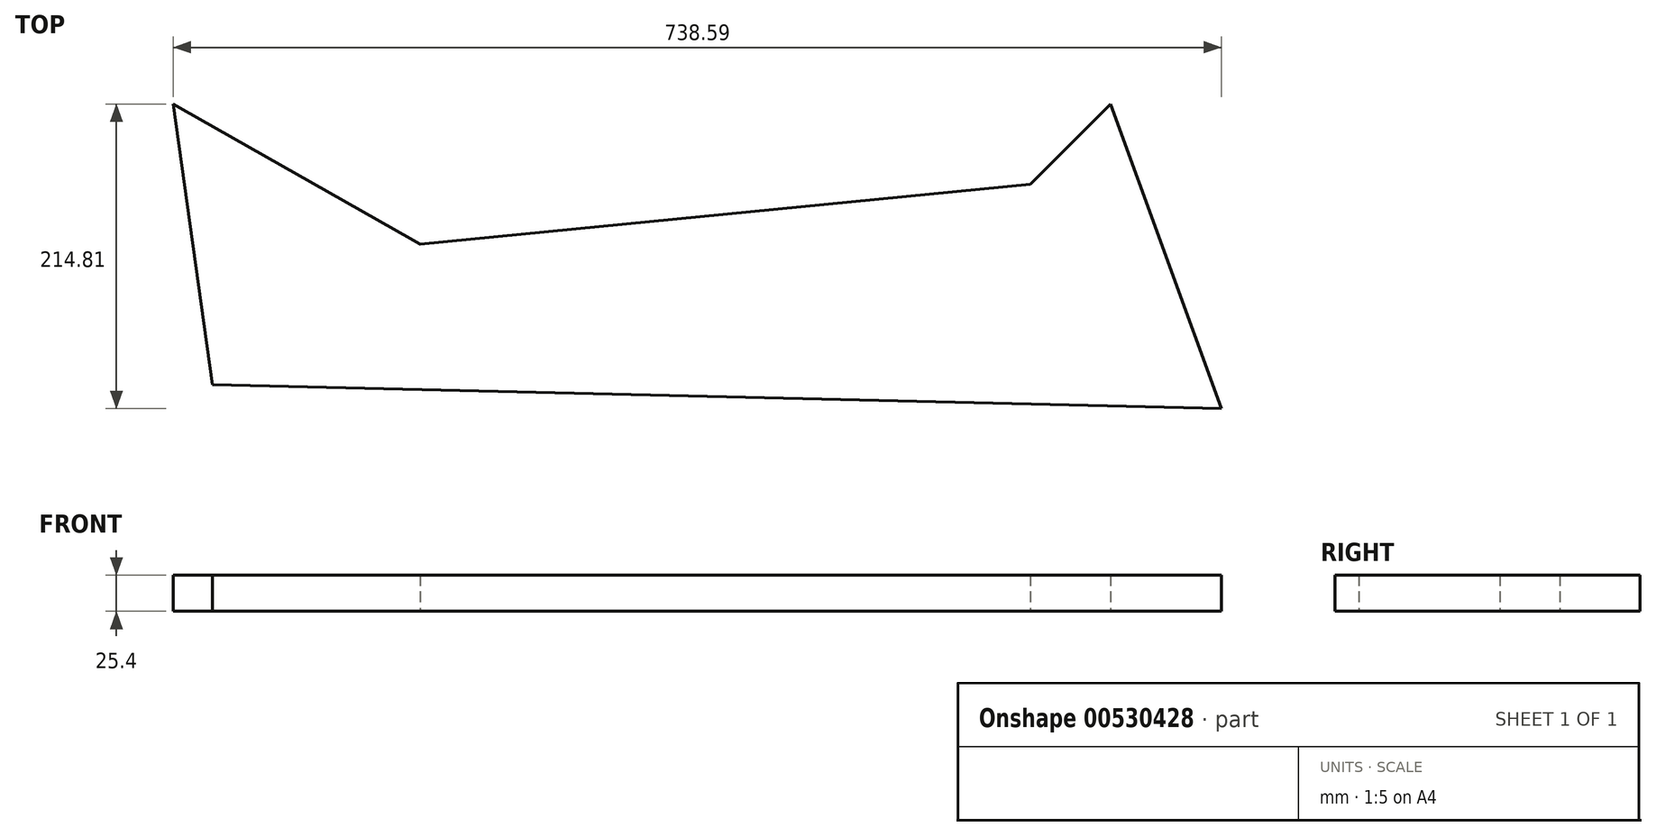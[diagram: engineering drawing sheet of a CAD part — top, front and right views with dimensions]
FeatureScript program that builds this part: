
annotation { "Feature Type Name" : "Feature", "Feature Type Description" : "" }
export const myFeature = defineFeature(function(context is Context, id is Id, definition is map)
    precondition{}
    {
        {
            var Q0;
            Q0=qCreatedBy(makeId("Top.planeOp"),FACE);
            var sketch = newSketch(context, id + "F0", { "sketchPlane" : qUnion([Q0])});
            skLineSegment(sketch, "E0", {"start": v(0, 0) * mm, "end": v(27.58, -198.09) * mm});
            skLineSegment(sketch, "E1", {"start": v(27.58, -198.09) * mm, "end": v(738.59, -214.81) * mm});
            skLineSegment(sketch, "E2", {"start": v(0, 0) * mm, "end": v(660.4, 0) * mm, "construction": true});
            skLineSegment(sketch, "E3", {"start": v(738.59, -214.81) * mm, "end": v(632.63, 76.3) * mm});
            skLineSegment(sketch, "E4", {"start": v(0, 0) * mm, "end": v(173.9, -98.79) * mm});
            skLineSegment(sketch, "E5", {"start": v(173.9, -98.79) * mm, "end": v(603.83, -56.57) * mm});
            skLineSegment(sketch, "E6", {"start": v(603.83, -56.57) * mm, "end": v(660.4, 0) * mm});
            skSolve(sketch);
        }
        {
            var Q0;
            Q0=qCreatedBy(makeId("Right.planeOp"),FACE);
            var sketch = newSketch(context, id + "F1", { "sketchPlane" : qUnion([Q0])});
            skSolve(sketch);
        }
        {
            var Q0;
            Q0 = qSketchRegion(id + "F0", true);
            var Q1;
            Q1 = qSketchRegion(id + "F1", true);
            extrude(context, id + "F2", {"entities" : qUnion([Q0, Q1]), "depth" : 25.4 * mm, "offsetDistance" : 25.4 * mm});
        }
    });
